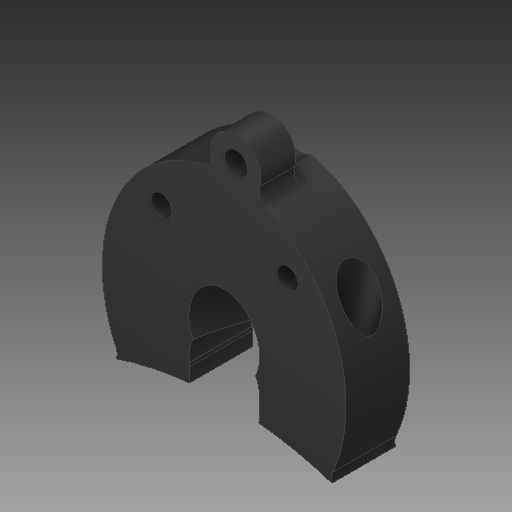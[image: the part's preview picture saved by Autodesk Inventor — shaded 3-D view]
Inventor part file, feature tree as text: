
AUTODESK INVENTOR PART (.ipt)
format: ipt  version: 2019 (Build 230136000, 136)  size: 329,216 bytes
history: native  units: mm
features: sketch x11, extrude x7, other x6, hole x4, fillet x3, plane x2, projected_geometry x2, revolve x1, mirror x1
ambient origin geometry x8: Origin, YZ Plane, XZ Plane, XY Plane, X Axis, Y Axis, Z Axis, Center Point
bodies: Solid1 (feature_tree)
feature tree (37):
  plane  "Work Plane1"
  extrude  "Extrusion1"  Depth=58.0mm
  extrude  "Extrusion2"  Depth=15.101mm TaperAngle=0.0deg
  extrude  "Extrusion3"  Depth=163.323mm
  fillet  "Fillet1"  [1 undecoded]
  fillet  "Fillet2"  Radius=0.20944mm
  hole  "Hole1"  [1 undecoded]
  extrude  "Extrusion4"  Depth=0.2mm
  extrude  "Extrusion5"  Depth=10.5mm
  other  "Work Point1"
  revolve  "Revolution1"  [1 undecoded]
  other  "Work Point2"
  hole  "Hole2"  [1 undecoded]
  extrude  "Extrusion6"  Depth=8.5mm TaperAngle=0.0deg
  fillet  "Fillet3"  Radius=10.646508mm
  hole  "Hole3"  [1 undecoded]
  sketch  "Sketch11"  dims[d39=16.867mm d40=22.866mm d41=25.830873mm d42=14.185526mm d43=90.0deg d44=10.0mm d45=10.0mm d46=16.867mm d47=6.0mm d48=4.0mm d49=2.0mm d50=90.0deg d51=8.0mm d52=20.594885mm d53=1.412mm d54=11.959mm d55=7.688mm d56=9.77mm d57=9.77mm d58=7.688mm d59=8.5mm d60=0.0mm d61=3.2mm d62=115.401mm d63=30.0mm d64=5.0mm d65=6.0mm d66=4.0mm d67=2.0mm d68=90.0deg d69=8.0mm d70=20.594885mm d71=2.155482mm d72=88.616mm d73=10.0mm d74=10.0mm d75=5.0mm d76=6.0mm d77=8.9mm d78=1.0mm d79=90.0deg d80=8.0mm d81=20.594885mm]
  other  "Work Axis2"
  other  "Work Point3"
  hole  "Hole4"  [1 undecoded]
  mirror  "Mirror1"
  sketch  "Sketch1"  dims[d0=5.061455mm d1=58.0mm]
  other  "Srf1"
  sketch  "Sketch2"  dims[d2=100.0mm d3=0.0mm d4=15.101mm d5=0.0mm]
  sketch  "Sketch3"  dims[d6=95.049mm d8=163.323mm d9=0.0mm d10=0.0mm d12=0.20944mm]
  sketch  "Sketch4"  dims[d13=132.0mm d14=12.0mm]
  sketch  "Sketch5"  dims[d15=8.5mm d16=0.0mm d17=0.2mm]
  sketch  "Sketch6"  dims[d18=3.2mm]
  sketch  "Sketch7"  dims[d19=5.4mm d20=6.0mm d21=4.0mm d22=2.0mm d23=90.0deg d24=8.0mm d25=20.594885mm d26=10.5mm]
  sketch  "Sketch8"  dims[d27=8.5mm d28=0.0mm d30=25.6275mm]
  other  "Work Axis1"
  sketch  "Sketch9"  dims[d31=25.6275mm d34=3.2mm]
  sketch  "Sketch10"  dims[d35=3.2mm d36=8.5mm d37=0.0mm d38=10.646508mm]
  plane  "Work Plane2"
  extrude  "ExtrusionSrf1"  Depth=10.0mm
  projected_geometry  "Project Cut Edges1"
  projected_geometry  "Project Cut Edges2"
note: 6 required parameter values undecoded (feature->parameter linkage not recoverable at this tier; creation-order binding heuristic only, values carry confidence <= 0.55)